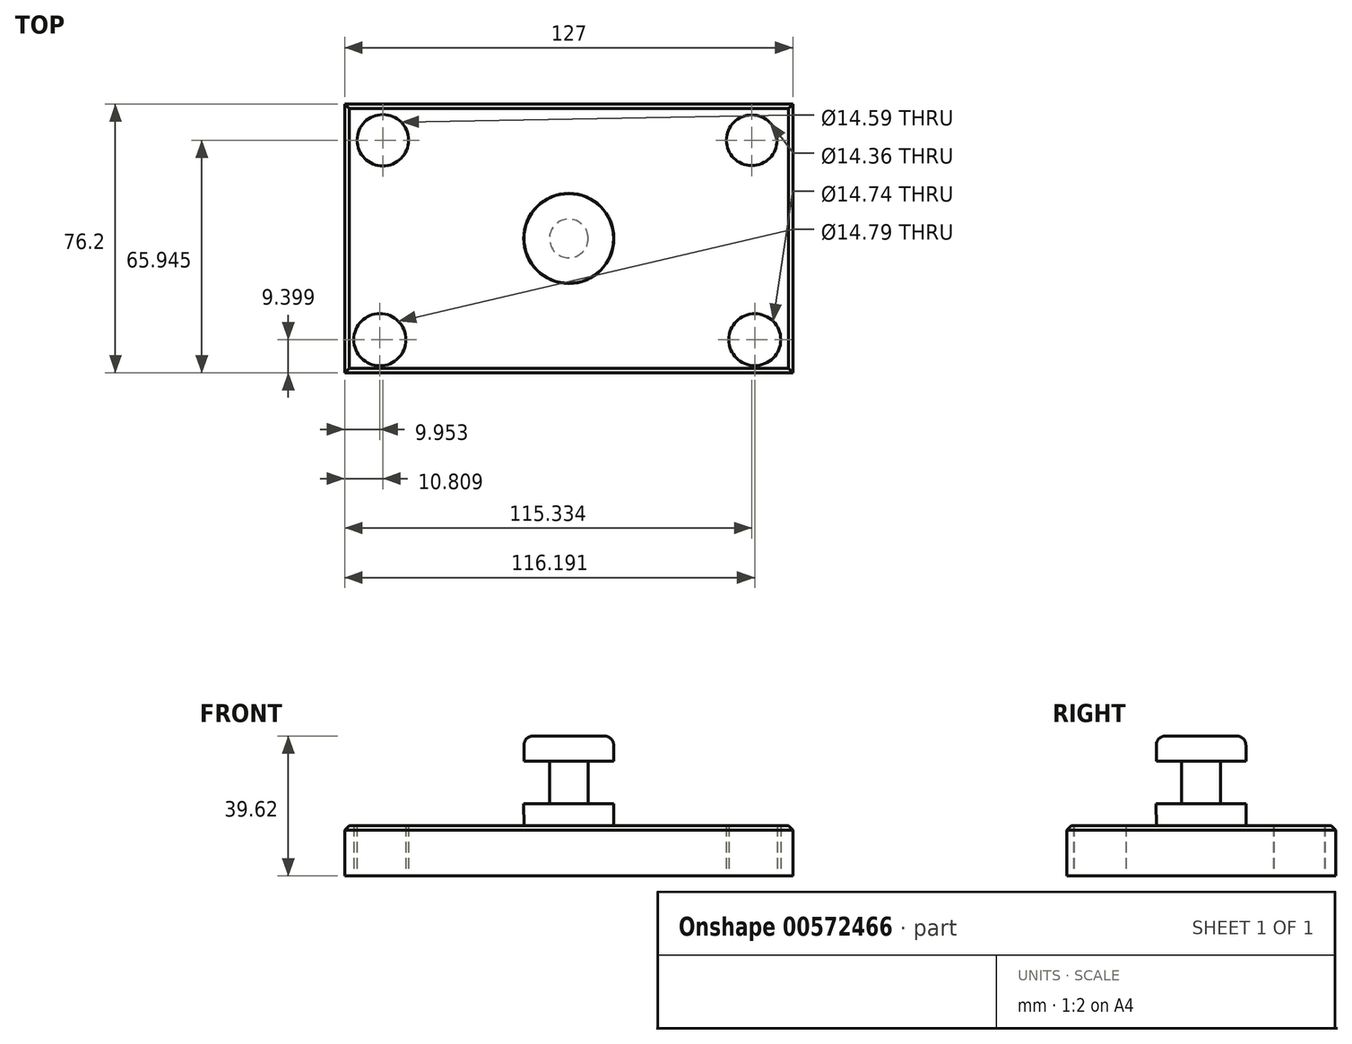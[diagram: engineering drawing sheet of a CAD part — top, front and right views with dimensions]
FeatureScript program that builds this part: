
annotation { "Feature Type Name" : "Feature", "Feature Type Description" : "" }
export const myFeature = defineFeature(function(context is Context, id is Id, definition is map)
    precondition{}
    {
        {
            var Q0;
            Q0=qCreatedBy(makeId("Top.planeOp"),FACE);
            var sketch = newSketch(context, id + "F0", { "sketchPlane" : qUnion([Q0])});
            skLineSegment(sketch, "E0.bottom", {"start": v(-63.5, 38.1) * mm, "end": v(63.5, 38.1) * mm});
            skLineSegment(sketch, "E0.top", {"start": v(-63.5, -38.1) * mm, "end": v(63.5, -38.1) * mm});
            skLineSegment(sketch, "E0.left", {"start": v(-63.5, 38.1) * mm, "end": v(-63.5, -38.1) * mm});
            skLineSegment(sketch, "E0.right", {"start": v(63.5, 38.1) * mm, "end": v(63.5, -38.1) * mm});
            skPoint(sketch, "E0.middle", {"position": v(0, 0) * mm});
            skSolve(sketch);
        }
        {
            var Q0;
            Q0=makeQuery(id+"F0.imprint","IMPRINT",FACE,{"disambiguationData":[TD([[makeQuery(id+"F0.imprint","IMPRINT",EDGE,{"derivedFrom":sQuery(id+"F0.wireOp",EDGE,"E0.bottom")}),-1.0]])]});
            extrude(context, id + "F1", {"entities" : qUnion([Q0]), "depth" : 14.22 * mm, "offsetDistance" : 25.4 * mm});
        }
        {
            var Q0;
            Q0=qCreatedBy(makeId("Top.planeOp"),FACE);
            var sketch = newSketch(context, id + "F2", { "sketchPlane" : qUnion([Q0])});
            skCircle(sketch, "E1", {"center": v(-52.7, 27.84) * mm, "radius": 7.3 * mm});
            skCircle(sketch, "E2", {"center": v(51.83, 27.84) * mm, "radius": 7.18 * mm});
            skCircle(sketch, "E3", {"center": v(52.7, -28.7) * mm, "radius": 7.37 * mm});
            skCircle(sketch, "E4", {"center": v(-53.55, -28.7) * mm, "radius": 7.4 * mm});
            skSolve(sketch);
        }
        {
            var Q0;
            Q0 = qSketchRegion(id + "F2", true);
            extrude(context, id + "F3", {"entities" : qUnion([Q0]), "operationType" : NewBodyOperationType.REMOVE, "depth" : 27.94 * mm, "offsetDistance" : 25.4 * mm});
        }
        {
            var Q0;
            Q0=qCreatedBy(makeId("Front.planeOp"),FACE);
            var sketch = newSketch(context, id + "F4", { "sketchPlane" : qUnion([Q0])});
            skLineSegment(sketch, "E5.bottom", {"start": v(0, 39.62) * mm, "end": v(12.7, 39.62) * mm});
            skLineSegment(sketch, "E5.top", {"start": v(0, 14.22) * mm, "end": v(12.7, 14.22) * mm});
            skLineSegment(sketch, "E5.left", {"start": v(0, 39.62) * mm, "end": v(0, 14.22) * mm});
            skLineSegment(sketch, "E6", {"start": v(12.7, 39.62) * mm, "end": v(12.7, 32.5) * mm});
            skLineSegment(sketch, "E7", {"start": v(12.7, 32.5) * mm, "end": v(5.5, 32.5) * mm});
            skLineSegment(sketch, "E8", {"start": v(5.5, 32.5) * mm, "end": v(5.5, 25.64) * mm});
            skLineSegment(sketch, "E9", {"start": v(5.5, 25.64) * mm, "end": v(5.5, 20.5) * mm});
            skLineSegment(sketch, "E10", {"start": v(5.5, 20.5) * mm, "end": v(12.78, 20.5) * mm});
            skLineSegment(sketch, "E11", {"start": v(12.78, 20.5) * mm, "end": v(12.7, 14.22) * mm});
            skSolve(sketch);
        }
        {
            var Q0;
            Q0=makeQuery(id+"F4.imprint","IMPRINT",FACE,{"disambiguationData":[TD([[makeQuery(id+"F4.imprint","IMPRINT",EDGE,{"derivedFrom":sQuery(id+"F4.wireOp",EDGE,"E5.bottom")}),-1.0]])]});
            var Q1;
            Q1=sQuery(id+"F4.wireOp",EDGE,"E5.left");
            revolve(context, id + "F5", {"operationType" : NewBodyOperationType.ADD, "entities" : qUnion([Q0]), "axis" : qUnion([Q1]), "revolveType" : RevolveType.FULL});
        }
        {
            var Q0;
            Q0=makeQuery(id+"F5.opRevolve","SWEPT_EDGE",EDGE,{"disambiguationData":[OSD([sQuery(id+"F4.wireOp",EDGE,"E5.bottom"),sQuery(id+"F4.wireOp",EDGE,"E6")])]});
            var Q1;
            Q1=makeQuery(id+"F5.opRevolve","SWEPT_EDGE",EDGE,{"disambiguationData":[OSD([sQuery(id+"F4.wireOp",EDGE,"E5.top"),sQuery(id+"F4.wireOp",EDGE,"E11")])]});
            fillet(context, id + "F6", {"entities" : qUnion([Q0, Q1]), "radius" : 2.54 * mm, "tangentPropagation" : true, "allowEdgeOverflow" : false});
        }
        {
            var Q0;
            Q0=makeQuery(id+"F1.opExtrude","CAP_EDGE",EDGE,{"disambiguationData":[OSD([sQuery(id+"F0.wireOp",EDGE,"E0.top")])],"isStart":false});
            var Q1;
            Q1=makeQuery(id+"F1.opExtrude","CAP_EDGE",EDGE,{"disambiguationData":[OSD([sQuery(id+"F0.wireOp",EDGE,"E0.right")])],"isStart":false});
            var Q2;
            Q2=makeQuery(id+"F1.opExtrude","CAP_EDGE",EDGE,{"disambiguationData":[OSD([sQuery(id+"F0.wireOp",EDGE,"E0.bottom")])],"isStart":false});
            var Q3;
            Q3=makeQuery(id+"F1.opExtrude","CAP_EDGE",EDGE,{"disambiguationData":[OSD([sQuery(id+"F0.wireOp",EDGE,"E0.left")])],"isStart":false});
            chamfer(context, id + "F7", {"entities" : qUnion([Q0, Q1, Q2, Q3]), "width" : 1.27 * mm, "tangentPropagation" : true});
        }
    });
